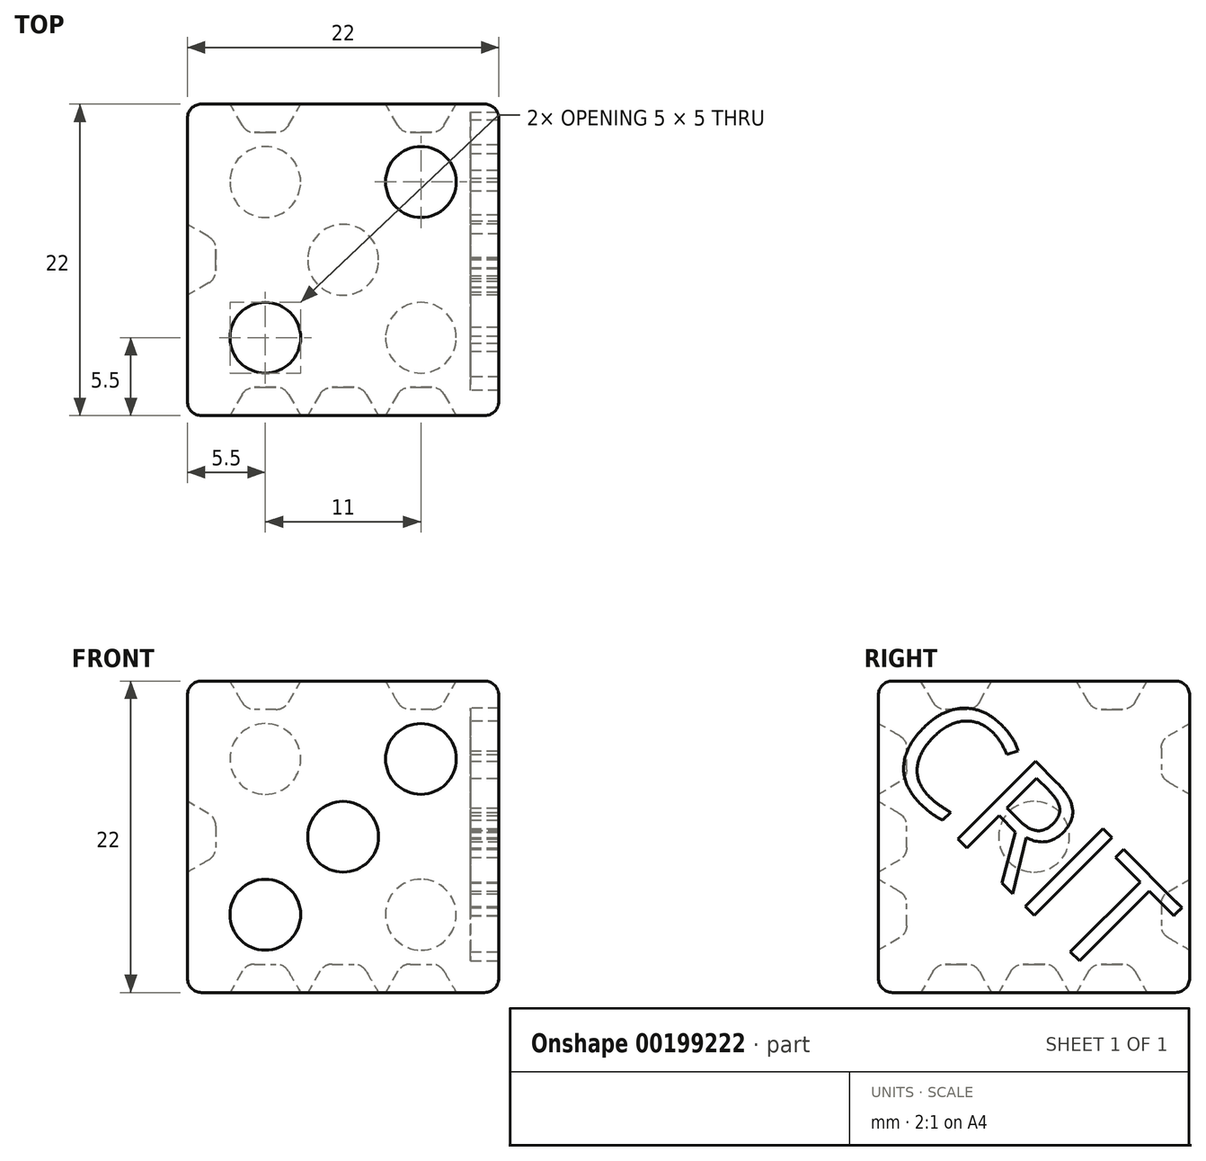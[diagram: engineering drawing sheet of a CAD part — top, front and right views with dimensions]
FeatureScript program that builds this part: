
annotation { "Feature Type Name" : "Feature", "Feature Type Description" : "" }
export const myFeature = defineFeature(function(context is Context, id is Id, definition is map)
    precondition{}
    {
        {
            var Q0;
            Q0=qCreatedBy(makeId("Top.planeOp"),FACE);
            var sketch = newSketch(context, id + "F0", { "sketchPlane" : qUnion([Q0])});
            skLineSegment(sketch, "E0.bottom", {"start": v(11, 11) * mm, "end": v(-11, 11) * mm});
            skLineSegment(sketch, "E0.top", {"start": v(11, -11) * mm, "end": v(-11, -11) * mm});
            skLineSegment(sketch, "E0.left", {"start": v(11, 11) * mm, "end": v(11, -11) * mm});
            skLineSegment(sketch, "E0.right", {"start": v(-11, 11) * mm, "end": v(-11, -11) * mm});
            skPoint(sketch, "E0.middle", {"position": v(0, 0) * mm});
            skSolve(sketch);
        }
        {
            var Q0;
            Q0=makeQuery(id+"F0.imprint","IMPRINT",FACE,{"disambiguationData":[TD([[makeQuery(id+"F0.imprint","IMPRINT",EDGE,{"derivedFrom":sQuery(id+"F0.wireOp",EDGE,"E0.bottom")}),1.0]])]});
            extrude(context, id + "F1", {"entities" : qUnion([Q0]), "depth" : 22 * mm});
        }
        {
            var Q0;
            Q0=makeQuery(id+"F1.opExtrude","SWEPT_FACE",FACE,{"disambiguationData":[OSD([sQuery(id+"F0.wireOp",EDGE,"E0.right")])]});
            var sketch = newSketch(context, id + "F2", { "sketchPlane" : qUnion([Q0])});
            skLineSegment(sketch, "E1", {"start": v(0, 22) * mm, "end": v(0, 0) * mm, "construction": true});
            skCircle(sketch, "E2", {"center": v(0, 11) * mm, "radius": 2.5 * mm});
            skSolve(sketch);
        }
        {
            var Q0;
            Q0=qSketchRegion(id+"F2",true);
            extrude(context, id + "F3", {"entities" : qUnion([Q0]), "operationType" : NewBodyOperationType.REMOVE, "oppositeDirection" : true, "depth" : 2 * mm, "hasDraft" : true, "draftAngle" : 30 * degree, "draftPullDirection" : true});
        }
        {
            var Q0;
            Q0=makeQuery(id+"F1.opExtrude","CAP_FACE",FACE,{"disambiguationData":[OSD([sQuery(id+"F0.wireOp",EDGE,"E0.bottom"),sQuery(id+"F0.wireOp",EDGE,"E0.top"),sQuery(id+"F0.wireOp",EDGE,"E0.left"),sQuery(id+"F0.wireOp",EDGE,"E0.right")])],"isStart":false});
            var sketch = newSketch(context, id + "F4", { "sketchPlane" : qUnion([Q0])});
            skLineSegment(sketch, "E3", {"start": v(11, 11) * mm, "end": v(-11, -11) * mm, "construction": true});
            skLineSegment(sketch, "E4", {"start": v(11, 11) * mm, "end": v(11, 0) * mm, "construction": true});
            skLineSegment(sketch, "E5", {"start": v(11, 0) * mm, "end": v(-11, 0) * mm, "construction": true});
            skLineSegment(sketch, "E6", {"start": v(-11, 0) * mm, "end": v(-11, -11) * mm, "construction": true});
            skLineSegment(sketch, "E7", {"start": v(-11, -5.5) * mm, "end": v(11, -5.5) * mm, "construction": true});
            skLineSegment(sketch, "E8", {"start": v(11, 5.5) * mm, "end": v(-11, 5.5) * mm, "construction": true});
            skCircle(sketch, "E9", {"center": v(5.5, 5.5) * mm, "radius": 2.5 * mm});
            skCircle(sketch, "E10", {"center": v(-5.5, -5.5) * mm, "radius": 2.5 * mm});
            skSolve(sketch);
        }
        {
            var Q0;
            Q0=qSketchRegion(id+"F4",true);
            extrude(context, id + "F5", {"entities" : qUnion([Q0]), "operationType" : NewBodyOperationType.REMOVE, "oppositeDirection" : true, "depth" : 2 * mm, "hasDraft" : true, "draftAngle" : 30 * degree, "draftPullDirection" : true});
        }
        {
            var Q0;
            Q0=makeQuery(id+"F1.opExtrude","SWEPT_FACE",FACE,{"disambiguationData":[OSD([sQuery(id+"F0.wireOp",EDGE,"E0.top")])]});
            var sketch = newSketch(context, id + "F6", { "sketchPlane" : qUnion([Q0])});
            skLineSegment(sketch, "E11", {"start": v(11, 11) * mm, "end": v(-11, 11) * mm, "construction": true});
            skLineSegment(sketch, "E12", {"start": v(11, 22) * mm, "end": v(0, 11) * mm, "construction": true});
            skLineSegment(sketch, "E13", {"start": v(0, 11) * mm, "end": v(-11, 0) * mm, "construction": true});
            skCircle(sketch, "E14", {"center": v(5.5, 16.5) * mm, "radius": 2.5 * mm});
            skCircle(sketch, "E15", {"center": v(0, 11) * mm, "radius": 2.5 * mm});
            skCircle(sketch, "E16", {"center": v(-5.5, 5.5) * mm, "radius": 2.5 * mm});
            skSolve(sketch);
        }
        {
            var Q0;
            Q0=qSketchRegion(id+"F6",true);
            extrude(context, id + "F7", {"entities" : qUnion([Q0]), "operationType" : NewBodyOperationType.REMOVE, "oppositeDirection" : true, "depth" : 2 * mm, "hasDraft" : true, "draftAngle" : 30 * degree, "draftPullDirection" : true});
        }
        {
            var Q0;
            Q0=makeQuery(id+"F1.opExtrude","SWEPT_FACE",FACE,{"disambiguationData":[OSD([sQuery(id+"F0.wireOp",EDGE,"E0.bottom")])]});
            var sketch = newSketch(context, id + "F8", { "sketchPlane" : qUnion([Q0])});
            skLineSegment(sketch, "E17", {"start": v(-11, 22) * mm, "end": v(11, 22) * mm, "construction": true});
            skLineSegment(sketch, "E18", {"start": v(0, 22) * mm, "end": v(0, 11) * mm, "construction": true});
            skPoint(sketch, "E18.endSnap0", {"position": v(-11, 11) * mm});
            skLineSegment(sketch, "E19", {"start": v(0, 11) * mm, "end": v(0, 0) * mm, "construction": true});
            skLineSegment(sketch, "E20", {"start": v(0, 11) * mm, "end": v(11, 11) * mm, "construction": true});
            skLineSegment(sketch, "E21", {"start": v(0, 22) * mm, "end": v(11, 11) * mm, "construction": true});
            skCircle(sketch, "E22", {"center": v(5.5, 16.5) * mm, "radius": 2.5 * mm});
            skCircle(sketch, "E23.MirrorC", {"center": v(-5.5, 16.5) * mm, "radius": 2.5 * mm});
            skCircle(sketch, "E24.MirrorC", {"center": v(5.5, 5.5) * mm, "radius": 2.5 * mm});
            skCircle(sketch, "E25.MirrorC", {"center": v(-5.5, 5.5) * mm, "radius": 2.5 * mm});
            skSolve(sketch);
        }
        {
            var Q0;
            Q0=qSketchRegion(id+"F8",true);
            extrude(context, id + "F9", {"entities" : qUnion([Q0]), "operationType" : NewBodyOperationType.REMOVE, "oppositeDirection" : true, "depth" : 2 * mm, "hasDraft" : true, "draftAngle" : 30 * degree, "draftPullDirection" : true});
        }
        {
            var Q0;
            Q0=makeQuery(id+"F1.opExtrude","CAP_FACE",FACE,{"disambiguationData":[OSD([sQuery(id+"F0.wireOp",EDGE,"E0.bottom"),sQuery(id+"F0.wireOp",EDGE,"E0.top"),sQuery(id+"F0.wireOp",EDGE,"E0.left"),sQuery(id+"F0.wireOp",EDGE,"E0.right")])],"isStart":true});
            var sketch = newSketch(context, id + "F10", { "sketchPlane" : qUnion([Q0])});
            skLineSegment(sketch, "E26", {"start": v(11, -11) * mm, "end": v(0, 0) * mm, "construction": true});
            skLineSegment(sketch, "E27", {"start": v(0, 0) * mm, "end": v(-11, 11) * mm, "construction": true});
            skLineSegment(sketch, "E28", {"start": v(11, 0) * mm, "end": v(-11, 0) * mm, "construction": true});
            skCircle(sketch, "E29", {"center": v(0, 0) * mm, "radius": 2.5 * mm});
            skCircle(sketch, "E30", {"center": v(5.5, -5.5) * mm, "radius": 2.5 * mm});
            skCircle(sketch, "E31", {"center": v(-5.5, 5.5) * mm, "radius": 2.5 * mm});
            skLineSegment(sketch, "E32", {"start": v(0, 0) * mm, "end": v(-11, -11) * mm, "construction": true});
            skLineSegment(sketch, "E33", {"start": v(0, 0) * mm, "end": v(11, 11) * mm, "construction": true});
            skCircle(sketch, "E34", {"center": v(5.5, 5.5) * mm, "radius": 2.5 * mm});
            skCircle(sketch, "E35", {"center": v(-5.5, -5.5) * mm, "radius": 2.5 * mm});
            skSolve(sketch);
        }
        {
            var Q0;
            Q0=qSketchRegion(id+"F10",true);
            extrude(context, id + "F11", {"entities" : qUnion([Q0]), "operationType" : NewBodyOperationType.REMOVE, "oppositeDirection" : true, "depth" : 2 * mm, "hasDraft" : true, "draftAngle" : 30 * degree, "draftPullDirection" : true});
        }
        {
            var Q0;
            Q0=makeQuery(id+"F1.opExtrude","SWEPT_FACE",FACE,{"disambiguationData":[OSD([sQuery(id+"F0.wireOp",EDGE,"E0.left")])]});
            var sketch = newSketch(context, id + "F12", { "sketchPlane" : qUnion([Q0])});
            skText(sketch, "E36", { "text": "CRIT\n", "fontName": "OpenSans-Regular.ttf"});
            skLineSegment(sketch, "E37", {"start": v(11, 0) * mm, "end": v(-11, 22) * mm, "construction": true});
            skLineSegment(sketch, "E38", {"start": v(-11, 0) * mm, "end": v(0, 11) * mm, "construction": true});
            skPoint(sketch, "E38.endSnap0", {"position": v(0, 11) * mm});
            const initialGuessF12  = {"E36": [-0.011, 0.01645, 0.7071, -0.7071, 0.00784]};
            skSetInitialGuess(sketch, initialGuessF12);
            skSolve(sketch);
        }
        {
            var Q0;
            Q0=qSketchRegion(id+"F12",true);
            extrude(context, id + "F13", {"entities" : qUnion([Q0]), "operationType" : NewBodyOperationType.REMOVE, "oppositeDirection" : true, "depth" : 2 * mm});
        }
        {
            var Q0;
            Q0=makeQuery(id+"F1.opExtrude","SWEPT_EDGE",EDGE,{"disambiguationData":[OSD([sQuery(id+"F0.wireOp",EDGE,"E0.top"),sQuery(id+"F0.wireOp",EDGE,"E0.left")])]});
            var Q1;
            Q1=makeQuery(id+"F1.opExtrude","CAP_EDGE",EDGE,{"disambiguationData":[OSD([sQuery(id+"F0.wireOp",EDGE,"E0.left")])],"isStart":true});
            var Q2;
            Q2=makeQuery(id+"F1.opExtrude","SWEPT_EDGE",EDGE,{"disambiguationData":[OSD([sQuery(id+"F0.wireOp",EDGE,"E0.bottom"),sQuery(id+"F0.wireOp",EDGE,"E0.left")])]});
            var Q3;
            Q3=makeQuery(id+"F1.opExtrude","CAP_EDGE",EDGE,{"disambiguationData":[OSD([sQuery(id+"F0.wireOp",EDGE,"E0.left")])],"isStart":false});
            var Q4;
            Q4=makeQuery(id+"F1.opExtrude","SWEPT_EDGE",EDGE,{"disambiguationData":[OSD([sQuery(id+"F0.wireOp",EDGE,"E0.top"),sQuery(id+"F0.wireOp",EDGE,"E0.right")])]});
            var Q5;
            Q5=makeQuery(id+"F1.opExtrude","CAP_EDGE",EDGE,{"disambiguationData":[OSD([sQuery(id+"F0.wireOp",EDGE,"E0.right")])],"isStart":true});
            var Q6;
            Q6=makeQuery(id+"F1.opExtrude","CAP_EDGE",EDGE,{"disambiguationData":[OSD([sQuery(id+"F0.wireOp",EDGE,"E0.top")])],"isStart":true});
            var Q7;
            Q7=makeQuery(id+"F1.opExtrude","CAP_EDGE",EDGE,{"disambiguationData":[OSD([sQuery(id+"F0.wireOp",EDGE,"E0.bottom")])],"isStart":true});
            var Q8;
            Q8=makeQuery(id+"F1.opExtrude","CAP_EDGE",EDGE,{"disambiguationData":[OSD([sQuery(id+"F0.wireOp",EDGE,"E0.top")])],"isStart":false});
            var Q9;
            Q9=makeQuery(id+"F1.opExtrude","SWEPT_EDGE",EDGE,{"disambiguationData":[OSD([sQuery(id+"F0.wireOp",EDGE,"E0.bottom"),sQuery(id+"F0.wireOp",EDGE,"E0.right")])]});
            var Q10;
            Q10=makeQuery(id+"F1.opExtrude","CAP_EDGE",EDGE,{"disambiguationData":[OSD([sQuery(id+"F0.wireOp",EDGE,"E0.bottom")])],"isStart":false});
            var Q11;
            Q11=makeQuery(id+"F1.opExtrude","CAP_EDGE",EDGE,{"disambiguationData":[OSD([sQuery(id+"F0.wireOp",EDGE,"E0.right")])],"isStart":false});
            var Q12;
            Q12=makeQuery(id+"F9.boolean.opBoolean","COPY",EDGE,{"derivedFrom":makeQuery(id+"F9.opExtrude","CAP_EDGE",EDGE,{"disambiguationData":[OSD([sQuery(id+"F8.wireOp",EDGE,"E22")])],"isStart":false})});
            var Q13;
            Q13=makeQuery(id+"F9.boolean.opBoolean","COPY",EDGE,{"derivedFrom":makeQuery(id+"F9.opExtrude","CAP_EDGE",EDGE,{"disambiguationData":[OSD([sQuery(id+"F8.wireOp",EDGE,"E24.MirrorC")])],"isStart":false})});
            var Q14;
            Q14=makeQuery(id+"F9.boolean.opBoolean","COPY",EDGE,{"derivedFrom":makeQuery(id+"F9.opExtrude","CAP_EDGE",EDGE,{"disambiguationData":[OSD([sQuery(id+"F8.wireOp",EDGE,"E25.MirrorC")])],"isStart":false})});
            var Q15;
            Q15=makeQuery(id+"F9.boolean.opBoolean","COPY",EDGE,{"derivedFrom":makeQuery(id+"F9.opExtrude","CAP_EDGE",EDGE,{"disambiguationData":[OSD([sQuery(id+"F8.wireOp",EDGE,"E23.MirrorC")])],"isStart":false})});
            var Q16;
            Q16=makeQuery(id+"F5.boolean.opBoolean","COPY",FACE,{"derivedFrom":makeQuery(id+"F5.opExtrude","CAP_FACE",FACE,{"disambiguationData":[OSD([sQuery(id+"F4.wireOp",EDGE,"E9")])],"isStart":false})});
            var Q17;
            Q17=makeQuery(id+"F5.boolean.opBoolean","COPY",EDGE,{"derivedFrom":makeQuery(id+"F5.opExtrude","CAP_EDGE",EDGE,{"disambiguationData":[OSD([sQuery(id+"F4.wireOp",EDGE,"E10")])],"isStart":false})});
            var Q18;
            Q18=makeQuery(id+"F11.boolean.opBoolean","COPY",FACE,{"derivedFrom":makeQuery(id+"F11.opExtrude","CAP_FACE",FACE,{"disambiguationData":[OSD([sQuery(id+"F10.wireOp",EDGE,"E35")])],"isStart":false})});
            var Q19;
            Q19=makeQuery(id+"F11.boolean.opBoolean","COPY",FACE,{"derivedFrom":makeQuery(id+"F11.opExtrude","CAP_FACE",FACE,{"disambiguationData":[OSD([sQuery(id+"F10.wireOp",EDGE,"E30")])],"isStart":false})});
            var Q20;
            Q20=makeQuery(id+"F11.boolean.opBoolean","COPY",FACE,{"derivedFrom":makeQuery(id+"F11.opExtrude","CAP_FACE",FACE,{"disambiguationData":[OSD([sQuery(id+"F10.wireOp",EDGE,"E29")])],"isStart":false})});
            var Q21;
            Q21=makeQuery(id+"F11.boolean.opBoolean","COPY",FACE,{"derivedFrom":makeQuery(id+"F11.opExtrude","CAP_FACE",FACE,{"disambiguationData":[OSD([sQuery(id+"F10.wireOp",EDGE,"E34")])],"isStart":false})});
            var Q22;
            Q22=makeQuery(id+"F11.boolean.opBoolean","COPY",FACE,{"derivedFrom":makeQuery(id+"F11.opExtrude","CAP_FACE",FACE,{"disambiguationData":[OSD([sQuery(id+"F10.wireOp",EDGE,"E31")])],"isStart":false})});
            var Q23;
            Q23=makeQuery(id+"F7.boolean.opBoolean","COPY",FACE,{"derivedFrom":makeQuery(id+"F7.opExtrude","CAP_FACE",FACE,{"disambiguationData":[OSD([sQuery(id+"F6.wireOp",EDGE,"E16")])],"isStart":false})});
            var Q24;
            Q24=makeQuery(id+"F7.boolean.opBoolean","COPY",EDGE,{"derivedFrom":makeQuery(id+"F7.opExtrude","CAP_EDGE",EDGE,{"disambiguationData":[OSD([sQuery(id+"F6.wireOp",EDGE,"E15")])],"isStart":false})});
            var Q25;
            Q25=makeQuery(id+"F3.boolean.opBoolean","COPY",EDGE,{"derivedFrom":makeQuery(id+"F3.opExtrude","CAP_EDGE",EDGE,{"disambiguationData":[OSD([sQuery(id+"F2.wireOp",EDGE,"E2")])],"isStart":false})});
            var Q26;
            Q26=makeQuery(id+"F7.boolean.opBoolean","COPY",EDGE,{"derivedFrom":makeQuery(id+"F7.opExtrude","CAP_EDGE",EDGE,{"disambiguationData":[OSD([sQuery(id+"F6.wireOp",EDGE,"E14")])],"isStart":false})});
            fillet(context, id + "F14", {"entities" : qUnion([Q0, Q1, Q2, Q3, Q4, Q5, Q6, Q7, Q8, Q9, Q10, Q11, Q12, Q13, Q14, Q15, Q16, Q17, Q18, Q19, Q20, Q21, Q22, Q23, Q24, Q25, Q26]), "radius" : 1 * mm, "tangentPropagation" : true, "allowEdgeOverflow" : false});
        }
    });
